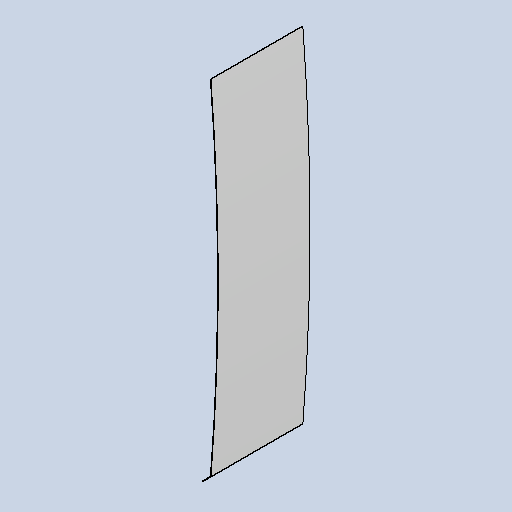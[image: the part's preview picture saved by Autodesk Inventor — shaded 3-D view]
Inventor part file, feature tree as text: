
AUTODESK INVENTOR PART (.ipt)
format: ipt  version: 2025 (Build 290162010, 162A)  size: 333,312 bytes
history: native  units: mm
features: other x4, sheet_metal_op x3, sketch x2
ambient origin geometry x8: Origin, YZ Plane, XZ Plane, XY Plane, X Axis, Y Axis, Z Axis, Center Point
bodies: Body1 (feature_tree)
feature tree (9):
  sheet_metal_op  "Contour Flange2"
  other  "Mark3"
  other  "A-Side Definition"
  sketch  "Sketch1"  dims[d36=3.0mm]
  other  "Plate2"
  sheet_metal_op  "Bend2"
  sheet_metal_op  "Corner2"
  sketch  "Sketch4"  dims[d37=3.0mm d38=1.5mm d39=6.0mm d40=5.0mm d41=492.0mm d42=5.0mm d43=3.0mm d44=12.0mm d45=3.0mm d46=5.0mm d65=8.0mm d78=3.0mm d80=3.0mm d148=5.0mm d153=63.0mm d165=11050.0mm d167=23.736478mm d169=1843.0mm d170=0.0mm]
  other  "Definition1"
